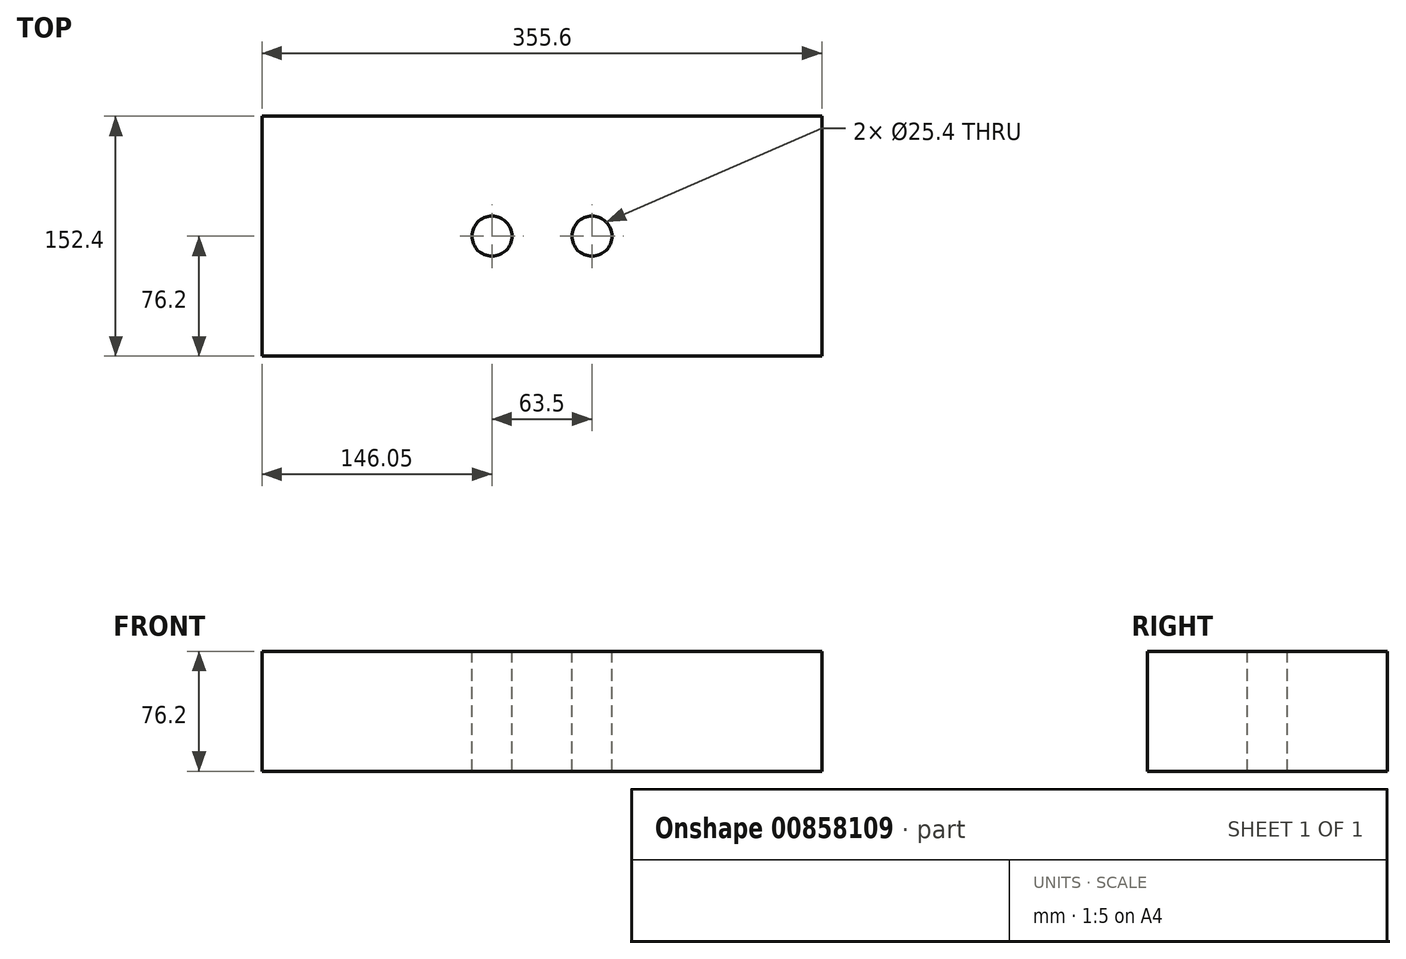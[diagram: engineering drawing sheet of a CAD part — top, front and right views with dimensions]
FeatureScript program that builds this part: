
annotation { "Feature Type Name" : "Feature", "Feature Type Description" : "" }
export const myFeature = defineFeature(function(context is Context, id is Id, definition is map)
    precondition{}
    {
        {
            var Q0;
            Q0=qCreatedBy(makeId("Top.planeOp"),FACE);
            var sketch = newSketch(context, id + "F0", { "sketchPlane" : qUnion([Q0])});
            skLineSegment(sketch, "E0.bottom", {"start": v(-177.8, 76.2) * mm, "end": v(177.8, 76.2) * mm});
            skLineSegment(sketch, "E0.top", {"start": v(-177.8, -76.2) * mm, "end": v(177.8, -76.2) * mm});
            skLineSegment(sketch, "E0.left", {"start": v(-177.8, 76.2) * mm, "end": v(-177.8, -76.2) * mm});
            skLineSegment(sketch, "E0.right", {"start": v(177.8, 76.2) * mm, "end": v(177.8, -76.2) * mm});
            skSolve(sketch);
        }
        {
            var Q0;
            Q0=makeQuery(id+"F0.imprint","IMPRINT",FACE,{"disambiguationData":[TD([[makeQuery(id+"F0.imprint","IMPRINT",EDGE,{"derivedFrom":sQuery(id+"F0.wireOp",EDGE,"E0.bottom")}),-1.0]])]});
            extrude(context, id + "F1", {"entities" : qUnion([Q0]), "depth" : 76.2 * mm, "offsetDistance" : 25.4 * mm});
        }
        {
            var Q0;
            Q0=makeQuery(id+"F1.opExtrude","CAP_FACE",FACE,{"disambiguationData":[OSD([sQuery(id+"F0.wireOp",EDGE,"E0.bottom"),sQuery(id+"F0.wireOp",EDGE,"E0.top"),sQuery(id+"F0.wireOp",EDGE,"E0.left"),sQuery(id+"F0.wireOp",EDGE,"E0.right")])],"isStart":false});
            var sketch = newSketch(context, id + "F2", { "sketchPlane" : qUnion([Q0])});
            skCircle(sketch, "E1", {"center": v(-31.75, 0) * mm, "radius": 12.7 * mm});
            skCircle(sketch, "E2", {"center": v(31.75, 0) * mm, "radius": 12.7 * mm});
            skSolve(sketch);
        }
        {
            var Q0;
            Q0=makeQuery(id+"F2.imprint","IMPRINT",FACE,{"disambiguationData":[TD([[makeQuery(id+"F2.imprint","IMPRINT",EDGE,{"derivedFrom":sQuery(id+"F2.wireOp",EDGE,"E1")}),1.0]])]});
            var Q1;
            Q1=makeQuery(id+"F2.imprint","IMPRINT",FACE,{"disambiguationData":[TD([[makeQuery(id+"F2.imprint","IMPRINT",EDGE,{"derivedFrom":sQuery(id+"F2.wireOp",EDGE,"E2")}),1.0]])]});
            extrude(context, id + "F3", {"entities" : qUnion([Q0, Q1]), "operationType" : NewBodyOperationType.REMOVE, "endBound" : BoundingType.UP_TO_NEXT, "oppositeDirection" : true, "depth" : 25.4 * mm, "offsetDistance" : 25.4 * mm});
        }
    });
